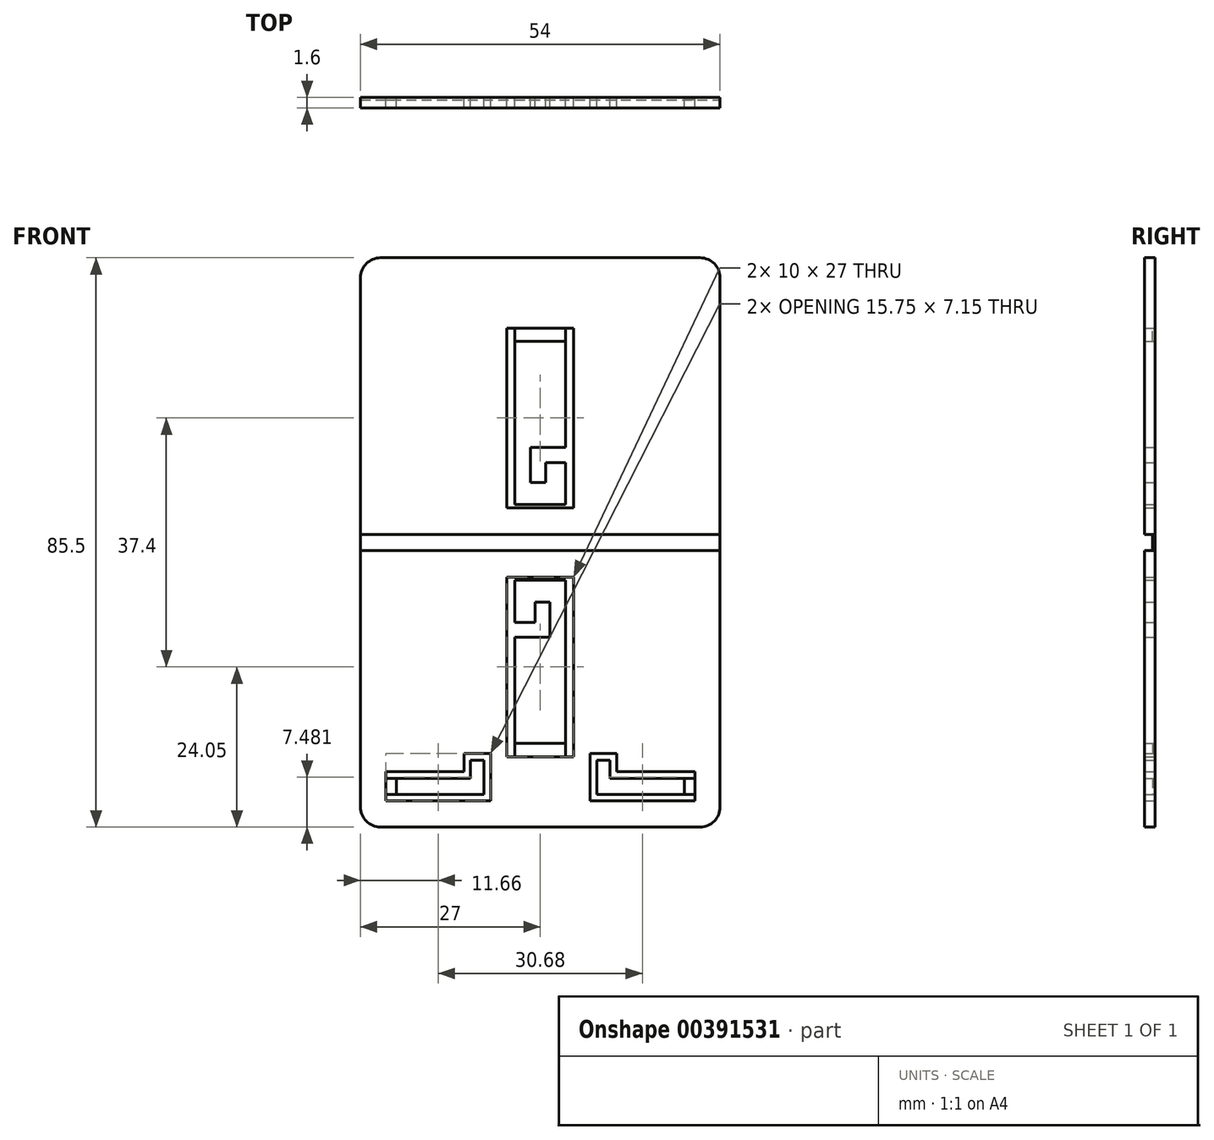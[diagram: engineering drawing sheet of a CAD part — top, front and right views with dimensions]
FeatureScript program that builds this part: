
annotation { "Feature Type Name" : "Feature", "Feature Type Description" : "" }
export const myFeature = defineFeature(function(context is Context, id is Id, definition is map)
    precondition{}
    {
        {
            var Q0;
            Q0=qCreatedBy(makeId("Front.planeOp"),FACE);
            var sketch = newSketch(context, id + "F0", { "sketchPlane" : qUnion([Q0])});
            skLineSegment(sketch, "E0.bottom", {"start": v(-3, 0) * mm, "end": v(-51, 0) * mm});
            skLineSegment(sketch, "E0.top", {"start": v(-3, 85.5) * mm, "end": v(-51, 85.5) * mm});
            skLineSegment(sketch, "E0.left", {"start": v(0, 3) * mm, "end": v(0, 82.5) * mm});
            skLineSegment(sketch, "E0.right", {"start": v(-54, 3) * mm, "end": v(-54, 82.5) * mm});
            skPoint(sketch, "E1.visualSharp", {"position": v(-54, 85.5) * mm});
            skArc(sketch, "E1.filletArc", {"start": v(-51, 85.5) * mm, "mid": v(-53.12, 84.62) * mm, "end": v(-54, 82.5) * mm});
            skPoint(sketch, "E2.visualSharp", {"position": v(0, 85.5) * mm});
            skArc(sketch, "E2.filletArc", {"start": v(0, 82.5) * mm, "mid": v(-0.88, 84.62) * mm, "end": v(-3, 85.5) * mm});
            skPoint(sketch, "E3.visualSharp", {"position": v(0, 0) * mm});
            skArc(sketch, "E3.filletArc", {"start": v(-3, 0) * mm, "mid": v(-0.88, 0.88) * mm, "end": v(0, 3) * mm});
            skPoint(sketch, "E4.visualSharp", {"position": v(-54, 0) * mm});
            skArc(sketch, "E4.filletArc", {"start": v(-54, 3) * mm, "mid": v(-53.12, 0.88) * mm, "end": v(-51, 0) * mm});
            skLineSegment(sketch, "E5", {"start": v(-54, 42.75) * mm, "end": v(0, 42.75) * mm, "construction": true});
            skLineSegment(sketch, "E6", {"start": v(-54, 43.95) * mm, "end": v(0, 43.95) * mm});
            skLineSegment(sketch, "E7", {"start": v(-27, 85.5) * mm, "end": v(-27, 0) * mm, "construction": true});
            skLineSegment(sketch, "E8.bottom", {"start": v(-32, 74.95) * mm, "end": v(-22, 74.95) * mm});
            skLineSegment(sketch, "E8.top", {"start": v(-32, 47.95) * mm, "end": v(-22, 47.95) * mm});
            skLineSegment(sketch, "E8.left", {"start": v(-32, 74.95) * mm, "end": v(-32, 47.95) * mm});
            skLineSegment(sketch, "E8.right", {"start": v(-22, 74.95) * mm, "end": v(-22, 47.95) * mm});
            skLineSegment(sketch, "E9", {"start": v(-27, 74.95) * mm, "end": v(-27, 47.95) * mm, "construction": true});
            skLineSegment(sketch, "E10", {"start": v(-30.8, 72.95) * mm, "end": v(-23.2, 72.95) * mm});
            skLineSegment(sketch, "E11", {"start": v(-30.8, 72.95) * mm, "end": v(-30.8, 48.45) * mm});
            skLineSegment(sketch, "E12", {"start": v(-23.2, 72.95) * mm, "end": v(-23.2, 57) * mm});
            skLineSegment(sketch, "E13", {"start": v(-30.8, 48.45) * mm, "end": v(-23.2, 48.45) * mm});
            skLineSegment(sketch, "E14", {"start": v(-23.2, 54.75) * mm, "end": v(-26.2, 54.75) * mm});
            skLineSegment(sketch, "E15", {"start": v(-26.2, 54.75) * mm, "end": v(-26.2, 51.75) * mm});
            skLineSegment(sketch, "E16", {"start": v(-26.2, 51.75) * mm, "end": v(-28.45, 51.75) * mm});
            skLineSegment(sketch, "E17", {"start": v(-28.45, 51.75) * mm, "end": v(-28.45, 57) * mm});
            skLineSegment(sketch, "E18", {"start": v(-28.45, 57) * mm, "end": v(-23.2, 57) * mm});
            skLineSegment(sketch, "E19.trimOffspring", {"start": v(-23.2, 54.75) * mm, "end": v(-23.2, 48.45) * mm});
            skLineSegment(sketch, "E20.MirrorCS", {"start": v(-54, 41.55) * mm, "end": v(0, 41.55) * mm});
            skLineSegment(sketch, "E21.bottom", {"start": v(-32, 37.55) * mm, "end": v(-22, 37.55) * mm});
            skLineSegment(sketch, "E21.top", {"start": v(-32, 10.55) * mm, "end": v(-22, 10.55) * mm});
            skLineSegment(sketch, "E21.left", {"start": v(-32, 37.55) * mm, "end": v(-32, 10.55) * mm});
            skLineSegment(sketch, "E21.right", {"start": v(-22, 37.55) * mm, "end": v(-22, 10.55) * mm});
            skLineSegment(sketch, "E22", {"start": v(-30.8, 12.55) * mm, "end": v(-23.2, 12.55) * mm});
            skLineSegment(sketch, "E23.bottom", {"start": v(-30.8, 37.05) * mm, "end": v(-23.2, 37.05) * mm});
            skLineSegment(sketch, "E23.left", {"start": v(-30.8, 37.05) * mm, "end": v(-30.8, 30.75) * mm});
            skLineSegment(sketch, "E23.right", {"start": v(-23.2, 37.05) * mm, "end": v(-23.2, 12.55) * mm});
            skLineSegment(sketch, "E24", {"start": v(-30.8, 30.75) * mm, "end": v(-27.8, 30.75) * mm});
            skLineSegment(sketch, "E25", {"start": v(-27.8, 30.75) * mm, "end": v(-27.8, 33.75) * mm});
            skLineSegment(sketch, "E26", {"start": v(-27.8, 33.75) * mm, "end": v(-25.55, 33.75) * mm});
            skLineSegment(sketch, "E27", {"start": v(-25.55, 33.75) * mm, "end": v(-25.55, 28.5) * mm});
            skLineSegment(sketch, "E28", {"start": v(-25.55, 28.5) * mm, "end": v(-30.8, 28.5) * mm});
            skLineSegment(sketch, "E29.trimOffspring", {"start": v(-30.8, 28.5) * mm, "end": v(-30.8, 12.55) * mm});
            skLineSegment(sketch, "E30.bottom", {"start": v(-50.21, 8.3) * mm, "end": v(-48.61, 8.3) * mm});
            skLineSegment(sketch, "E30.top", {"start": v(-50.21, 3.9) * mm, "end": v(-34.46, 3.9) * mm});
            skLineSegment(sketch, "E30.left", {"start": v(-50.21, 8.3) * mm, "end": v(-50.21, 3.9) * mm});
            skLineSegment(sketch, "E30.right", {"start": v(-34.46, 11.06) * mm, "end": v(-34.46, 3.9) * mm});
            skLineSegment(sketch, "E31", {"start": v(-48.61, 7.3) * mm, "end": v(-48.61, 4.9) * mm});
            skLineSegment(sketch, "E32", {"start": v(-30.8, 12.55) * mm, "end": v(-30.8, 10.55) * mm});
            skLineSegment(sketch, "E33", {"start": v(-23.2, 10.55) * mm, "end": v(-23.2, 12.55) * mm});
            skLineSegment(sketch, "E34", {"start": v(-30.8, 72.95) * mm, "end": v(-30.8, 74.95) * mm});
            skLineSegment(sketch, "E35", {"start": v(-23.2, 72.95) * mm, "end": v(-23.2, 74.95) * mm});
            skLineSegment(sketch, "E36", {"start": v(-50.21, 7.3) * mm, "end": v(-37.46, 7.3) * mm});
            skLineSegment(sketch, "E37", {"start": v(-50.21, 4.9) * mm, "end": v(-35.46, 4.9) * mm});
            skLineSegment(sketch, "E38", {"start": v(-37.46, 7.3) * mm, "end": v(-37.46, 10.06) * mm});
            skLineSegment(sketch, "E39", {"start": v(-37.46, 10.06) * mm, "end": v(-35.46, 10.06) * mm});
            skLineSegment(sketch, "E40", {"start": v(-35.46, 10.06) * mm, "end": v(-35.46, 4.9) * mm});
            skLineSegment(sketch, "E41", {"start": v(-48.61, 8.3) * mm, "end": v(-38.46, 8.3) * mm});
            skLineSegment(sketch, "E42", {"start": v(-38.46, 8.3) * mm, "end": v(-38.46, 11.06) * mm});
            skLineSegment(sketch, "E43", {"start": v(-38.46, 11.06) * mm, "end": v(-34.46, 11.06) * mm});
            skLineSegment(sketch, "E44.MirrorCS", {"start": v(-15.54, 8.3) * mm, "end": v(-15.54, 11.06) * mm});
            skLineSegment(sketch, "E45.MirrorCS", {"start": v(-15.54, 11.06) * mm, "end": v(-19.54, 11.06) * mm});
            skLineSegment(sketch, "E46.MirrorCS", {"start": v(-3.79, 8.3) * mm, "end": v(-5.39, 8.3) * mm});
            skLineSegment(sketch, "E47.MirrorCS", {"start": v(-3.79, 7.3) * mm, "end": v(-16.54, 7.3) * mm});
            skLineSegment(sketch, "E48.MirrorCS", {"start": v(-19.54, 11.06) * mm, "end": v(-19.54, 3.9) * mm});
            skLineSegment(sketch, "E49.MirrorCS", {"start": v(-3.79, 4.9) * mm, "end": v(-18.54, 4.9) * mm});
            skLineSegment(sketch, "E50.MirrorCS", {"start": v(-3.79, 8.3) * mm, "end": v(-3.79, 3.9) * mm});
            skLineSegment(sketch, "E51.MirrorCS", {"start": v(-5.39, 7.3) * mm, "end": v(-5.39, 4.9) * mm});
            skLineSegment(sketch, "E52.MirrorCS", {"start": v(-16.54, 7.3) * mm, "end": v(-16.54, 10.06) * mm});
            skLineSegment(sketch, "E53.MirrorCS", {"start": v(-16.54, 10.06) * mm, "end": v(-18.54, 10.06) * mm});
            skLineSegment(sketch, "E54.MirrorCS", {"start": v(-5.39, 8.3) * mm, "end": v(-15.54, 8.3) * mm});
            skLineSegment(sketch, "E55.MirrorCS", {"start": v(-3.79, 3.9) * mm, "end": v(-19.54, 3.9) * mm});
            skLineSegment(sketch, "E56.MirrorCS", {"start": v(-18.54, 10.06) * mm, "end": v(-18.54, 4.9) * mm});
            skSolve(sketch);
        }
        {
            var Q0;
            {var subQ0=sQuery(id+"F0.wireOp",EDGE,"E6");Q0=makeQuery(id+"F0.imprint","IMPRINT",FACE,{"disambiguationData":[TD([[makeQuery(id+"F0.imprint","IMPRINT",EDGE,{"derivedFrom":subQ0}),-1.0]])]});}
            var Q1;
            Q1=makeQuery(id+"F0.imprint","IMPRINT",FACE,{"disambiguationData":[TD([[makeQuery(id+"F0.imprint","IMPRINT",EDGE,{"derivedFrom":sQuery(id+"F0.wireOp",EDGE,"E10")}),1.0]])]});
            var Q2;
            Q2=makeQuery(id+"F0.imprint","IMPRINT",FACE,{"disambiguationData":[TD([[makeQuery(id+"F0.imprint","IMPRINT",EDGE,{"derivedFrom":sQuery(id+"F0.wireOp",EDGE,"E22")}),-1.0]])]});
            var Q3;
            {var subQ3=sQuery(id+"F0.wireOp",EDGE,"E51.MirrorCS");Q3=makeQuery(id+"F0.imprint","IMPRINT",FACE,{"disambiguationData":[TD([[makeQuery(id+"F0.imprint","IMPRINT",EDGE,{"derivedFrom":subQ3}),1.0]])]});}
            var Q4;
            {var subQ5=sQuery(id+"F0.wireOp",EDGE,"E31");Q4=makeQuery(id+"F0.imprint","IMPRINT",FACE,{"disambiguationData":[TD([[makeQuery(id+"F0.imprint","IMPRINT",EDGE,{"derivedFrom":subQ5}),-1.0]])]});}
            extrude(context, id + "F1", {"entities" : qUnion([Q0, Q1, Q2, Q3, Q4]), "depth" : 0.4 * mm});
        }
        {
            var Q0;
            Q0=makeQuery(id+"F0.imprint","IMPRINT",FACE,{"disambiguationData":[TD([[makeQuery(id+"F0.imprint","IMPRINT",EDGE,{"derivedFrom":sQuery(id+"F0.wireOp",EDGE,"E0.top")}),1.0]])]});
            var Q1;
            Q1=makeQuery(id+"F0.imprint","IMPRINT",FACE,{"disambiguationData":[TD([[makeQuery(id+"F0.imprint","IMPRINT",EDGE,{"derivedFrom":sQuery(id+"F0.wireOp",EDGE,"E10")}),-1.0]])]});
            var Q2;
            Q2=makeQuery(id+"F0.imprint","IMPRINT",FACE,{"disambiguationData":[TD([[makeQuery(id+"F0.imprint","IMPRINT",EDGE,{"derivedFrom":sQuery(id+"F0.wireOp",EDGE,"E0.bottom")}),-1.0]])]});
            var Q3;
            Q3=makeQuery(id+"F0.imprint","IMPRINT",FACE,{"disambiguationData":[TD([[makeQuery(id+"F0.imprint","IMPRINT",EDGE,{"derivedFrom":sQuery(id+"F0.wireOp",EDGE,"E23.bottom")}),-1.0]])]});
            var Q4;
            {var subQ2=sQuery(id+"F0.wireOp",EDGE,"E31");Q4=makeQuery(id+"F0.imprint","IMPRINT",FACE,{"disambiguationData":[TD([[makeQuery(id+"F0.imprint","IMPRINT",EDGE,{"derivedFrom":subQ2}),1.0]])]});}
            var Q5;
            {var subQ0=sQuery(id+"F0.wireOp",EDGE,"E51.MirrorCS");Q5=makeQuery(id+"F0.imprint","IMPRINT",FACE,{"disambiguationData":[TD([[makeQuery(id+"F0.imprint","IMPRINT",EDGE,{"derivedFrom":subQ0}),-1.0]])]});}
            extrude(context, id + "F2", {"entities" : qUnion([Q0, Q1, Q2, Q3, Q4, Q5]), "depth" : 1.6 * mm});
        }
    });
